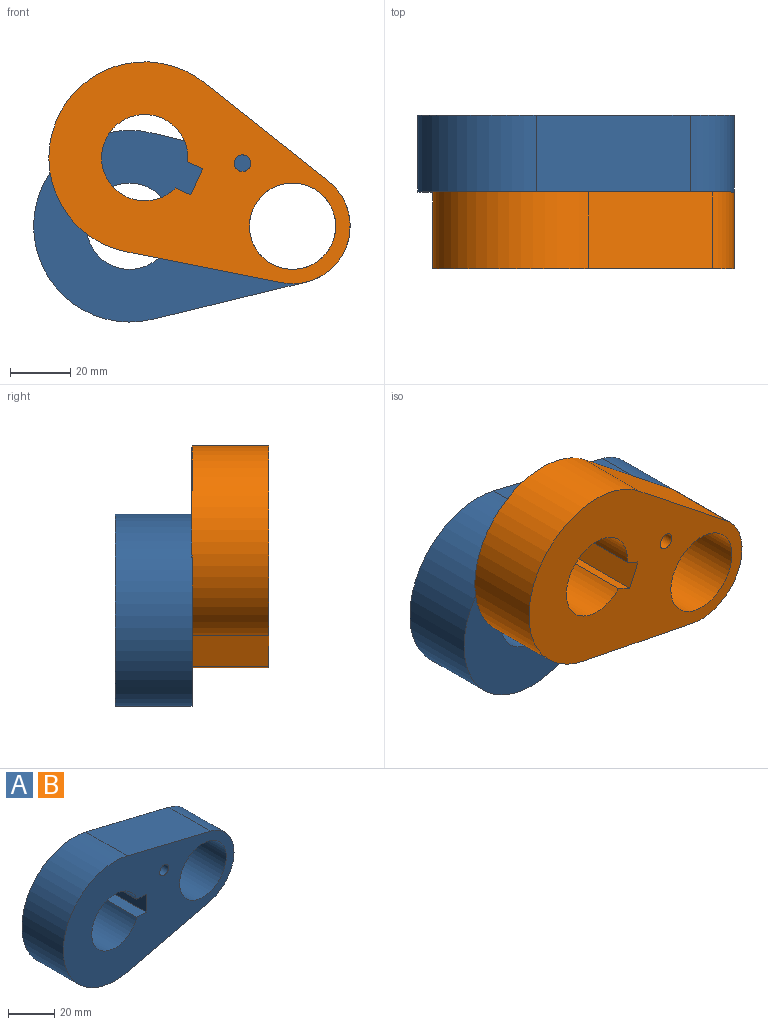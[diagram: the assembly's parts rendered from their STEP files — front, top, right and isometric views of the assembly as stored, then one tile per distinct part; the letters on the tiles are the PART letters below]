
ASSEMBLY  parts=2 mates=1
PART A: 12 faces, bbox 104.8x25.4x63.5 mm
  f0: cylinder r=31.75mm len=63.5mm, axis (0,1,0), area 2916.6mm2, adj f1,f6,f9,f10
  f1: plane 50.99x25.4mm, normal (0.24,0,-0.97), area 1332.5mm2, adj f0,f2,f9,f10
  f2: cylinder r=19.05mm len=37.03mm, axis (0,1,0), area 1290.3mm2, adj f1,f6,f9,f10
  f3: cylinder r=14.29mm len=28.58mm, axis (0,1,0), area 2033.5mm2, adj f4,f7,f9,f10
  f4: plane 25.4x5.58mm, normal (0,0,-1), area 141.7mm2, adj f3,f5,f9,f10
  f5: plane 25.4x9.53mm, normal (-1,0,0), area 241.9mm2, adj f4,f7,f9,f10
  f6: plane 50.99x25.4mm, normal (0.24,0,0.97), area 1332.5mm2, adj f0,f2,f9,f10
  f7: plane 25.4x5.58mm, normal (0,0,1), area 141.7mm2, adj f3,f5,f9,f10
  f8: cylinder r=14.29mm len=28.58mm, axis (0,1,0), area 2280.2mm2, adj f9,f10
  f9: plane 104.78x63.5mm, normal (0,-1,0), area 3617.4mm2, adj f0,f1,f2,f3,f4,f5,f6,f7
  f10: plane 104.78x63.5mm, normal (0,1,0), area 3617.4mm2, adj f0,f1,f2,f3,f4,f5,f6,f7
  f11: cylinder r=2.75mm len=25.4mm, axis (0,-1,0), area 438.9mm2, adj f9,f10
PART B: same geometry as A
PLACE A t=(20.84,44.84,38.04)mm fixed
PLACE B rot(axis=(0,1,0),24.9deg) t=(25.84,19.44,60.73)mm
MATE revolute B.f2 <-> A.f2  axis (0,1,0) through (74.81,19.44,38.04)mm
